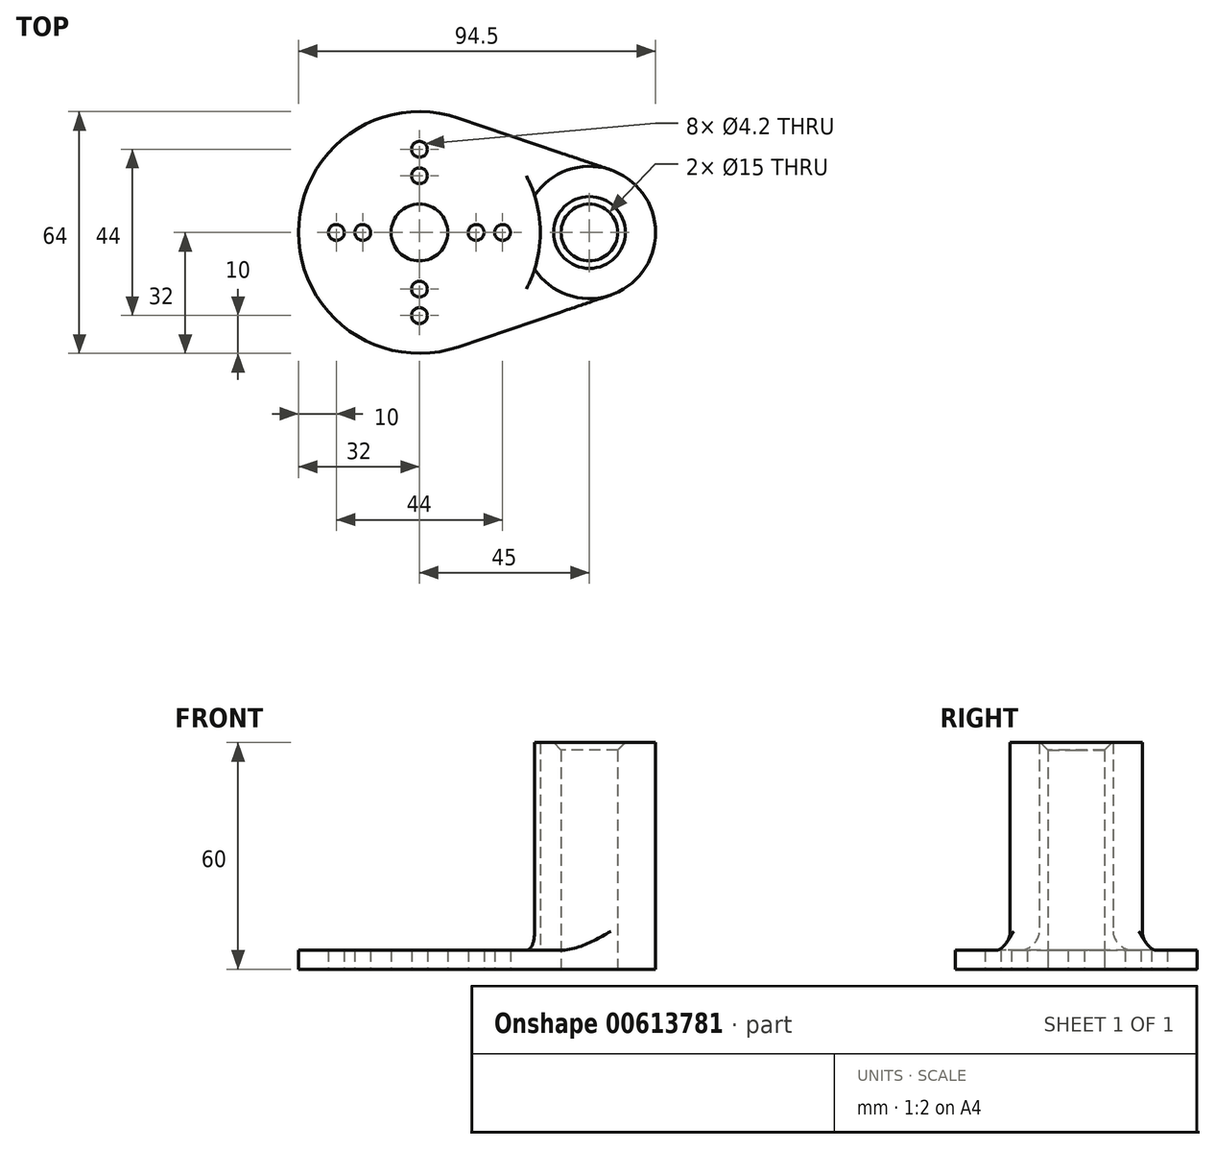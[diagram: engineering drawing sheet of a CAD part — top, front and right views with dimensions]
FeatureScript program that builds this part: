
annotation { "Feature Type Name" : "Feature", "Feature Type Description" : "" }
export const myFeature = defineFeature(function(context is Context, id is Id, definition is map)
    precondition{}
    {
        {
            var Q0;
            Q0=qCreatedBy(makeId("Top.planeOp"),FACE);
            var sketch = newSketch(context, id + "F0", { "sketchPlane" : qUnion([Q0])});
            skCircle(sketch, "E0", {"center": v(0, 0) * mm, "radius": 32 * mm});
            skCircle(sketch, "E1", {"center": v(45, 0) * mm, "radius": 17.5 * mm});
            skLineSegment(sketch, "E2", {"start": v(50.64, 16.57) * mm, "end": v(10.31, 30.3) * mm});
            skCircle(sketch, "E3", {"center": v(0, 22) * mm, "radius": 2.1 * mm});
            skLineSegment(sketch, "E4", {"start": v(-25, -19.97) * mm, "end": v(-25, -19.97) * mm});
            skLineSegment(sketch, "E5.MirrorCS", {"start": v(50.64, -16.57) * mm, "end": v(10.31, -30.3) * mm});
            skCircle(sketch, "E6", {"center": v(0, 15) * mm, "radius": 2.1 * mm});
            skCircle(sketch, "E7.1.0", {"center": v(-22, 0) * mm, "radius": 2.1 * mm});
            skCircle(sketch, "E7.1.1", {"center": v(-15, 0) * mm, "radius": 2.1 * mm});
            skCircle(sketch, "E7.2.0", {"center": v(0, -22) * mm, "radius": 2.1 * mm});
            skCircle(sketch, "E7.2.1", {"center": v(0, -15) * mm, "radius": 2.1 * mm});
            skCircle(sketch, "E7.3.0", {"center": v(22, 0) * mm, "radius": 2.1 * mm});
            skCircle(sketch, "E7.3.1", {"center": v(15, 0) * mm, "radius": 2.1 * mm});
            skCircle(sketch, "E8", {"center": v(45, 0) * mm, "radius": 7.5 * mm});
            skCircle(sketch, "E9", {"center": v(45, 0) * mm, "radius": 5 * mm});
            skCircle(sketch, "E10", {"center": v(0, 0) * mm, "radius": 7.5 * mm});
            skSolve(sketch);
        }
        {
            var Q0;
            Q0=makeQuery(id+"F0.imprint","IMPRINT",FACE,{"disambiguationData":[TD([[makeQuery(id+"F0.imprint","IMPRINT",EDGE,{"derivedFrom":sQuery(id+"F0.wireOp",EDGE,"E3")}),-1.0]])]});
            var Q1;
            {var subQ0=sQuery(id+"F0.wireOp",EDGE,"E2");Q1=makeQuery(id+"F0.imprint","IMPRINT",FACE,{"disambiguationData":[TD([[makeQuery(id+"F0.imprint","IMPRINT",EDGE,{"derivedFrom":subQ0}),1.0]])]});}
            var Q2;
            Q2=makeQuery(id+"F0.imprint","IMPRINT",FACE,{"disambiguationData":[TD([[makeQuery(id+"F0.imprint","IMPRINT",EDGE,{"derivedFrom":sQuery(id+"F0.wireOp",EDGE,"E8")}),-1.0]])]});
            var Q3;
            {var subQ0=sQuery(id+"F0.wireOp",EDGE,"E2");var subQ1=sQuery(id+"F0.wireOp",EDGE,"E0");var subQ2=makeQuery(id+"F0.imprint","INTERSECT",VERTEX,{"derivedFrom":[subQ1,subQ0]});Q3=makeQuery(id+"F0.imprint","IMPRINT",FACE,{"disambiguationData":[TD([[makeQuery(id+"F0.imprint","IMPRINT",EDGE,{"disambiguationData":[TD([[subQ2,-1.0]])],"derivedFrom":subQ1}),-1.0]])]});}
            var Q4;
            {var subQ0=sQuery(id+"F0.wireOp",EDGE,"E5.MirrorCS");Q4=makeQuery(id+"F0.imprint","IMPRINT",FACE,{"disambiguationData":[TD([[makeQuery(id+"F0.imprint","IMPRINT",EDGE,{"derivedFrom":subQ0}),-1.0]])]});}
            var Q5;
            {var subQ0=sQuery(id+"F0.wireOp",EDGE,"E0");var subQ1=sQuery(id+"F0.wireOp",EDGE,"E1");var subQ2=makeQuery(id+"F0.imprint","INTERSECT",VERTEX,{"disambiguationData":[OD(0.0)],"derivedFrom":[subQ1,subQ0]});Q5=makeQuery(id+"F0.imprint","IMPRINT",FACE,{"disambiguationData":[TD([[makeQuery(id+"F0.imprint","IMPRINT",EDGE,{"disambiguationData":[TD([[subQ2,-1.0]])],"derivedFrom":subQ1}),1.0]])]});}
            extrude(context, id + "F1", {"entities" : qUnion([Q0, Q1, Q2, Q3, Q4, Q5]), "depth" : 5 * mm, "offsetDistance" : 25 * mm});
        }
        {
            var Q0;
            Q0=makeQuery(id+"F0.imprint","IMPRINT",FACE,{"disambiguationData":[TD([[makeQuery(id+"F0.imprint","IMPRINT",EDGE,{"derivedFrom":sQuery(id+"F0.wireOp",EDGE,"E8")}),-1.0]])]});
            var Q1;
            Q1=sQuery(id+"F0.wireOp",EDGE,"E8");
            var Q2;
            Q2=sQuery(id+"F0.wireOp",EDGE,"E1");
            extrude(context, id + "F2", {"entities" : qUnion([Q0]), "operationType" : NewBodyOperationType.ADD, "surfaceEntities" : qUnion([Q1, Q2]), "depth" : 60 * mm, "offsetDistance" : 25 * mm});
        }
        {
            var Q0;
            {var subQ0=sQuery(id+"F0.wireOp",EDGE,"E1");Q0=makeQuery(id+"F2.boolean.opBoolean","INTERSECT",EDGE,{"derivedFrom":[makeQuery(id+"F1.opExtrude","CAP_FACE",FACE,{"disambiguationData":[OSD([sQuery(id+"F0.wireOp",EDGE,"E0"),subQ0,sQuery(id+"F0.wireOp",EDGE,"E2"),sQuery(id+"F0.wireOp",EDGE,"E3"),sQuery(id+"F0.wireOp",EDGE,"E5.MirrorCS"),sQuery(id+"F0.wireOp",EDGE,"E6"),sQuery(id+"F0.wireOp",EDGE,"E7.1.0"),sQuery(id+"F0.wireOp",EDGE,"E7.1.1"),sQuery(id+"F0.wireOp",EDGE,"E7.2.0"),sQuery(id+"F0.wireOp",EDGE,"E7.2.1"),sQuery(id+"F0.wireOp",EDGE,"E7.3.0"),sQuery(id+"F0.wireOp",EDGE,"E7.3.1"),sQuery(id+"F0.wireOp",EDGE,"E9")])],"isStart":false}),makeQuery(id+"F2.opExtrude","SWEPT_FACE",FACE,{"disambiguationData":[OSD([subQ0])]})]});}
            fillet(context, id + "F3", {"entities" : qUnion([Q0]), "radius" : 5 * mm, "tangentPropagation" : true, "allowEdgeOverflow" : false});
        }
        {
            var Q0;
            Q0=makeQuery(id+"F2.opExtrude","CAP_EDGE",EDGE,{"disambiguationData":[OSD([sQuery(id+"F0.wireOp",EDGE,"E8")])],"isStart":false});
            chamfer(context, id + "F5", {"entities" : qUnion([Q0]), "width" : 2 * mm, "tangentPropagation" : true});
        }
    });
